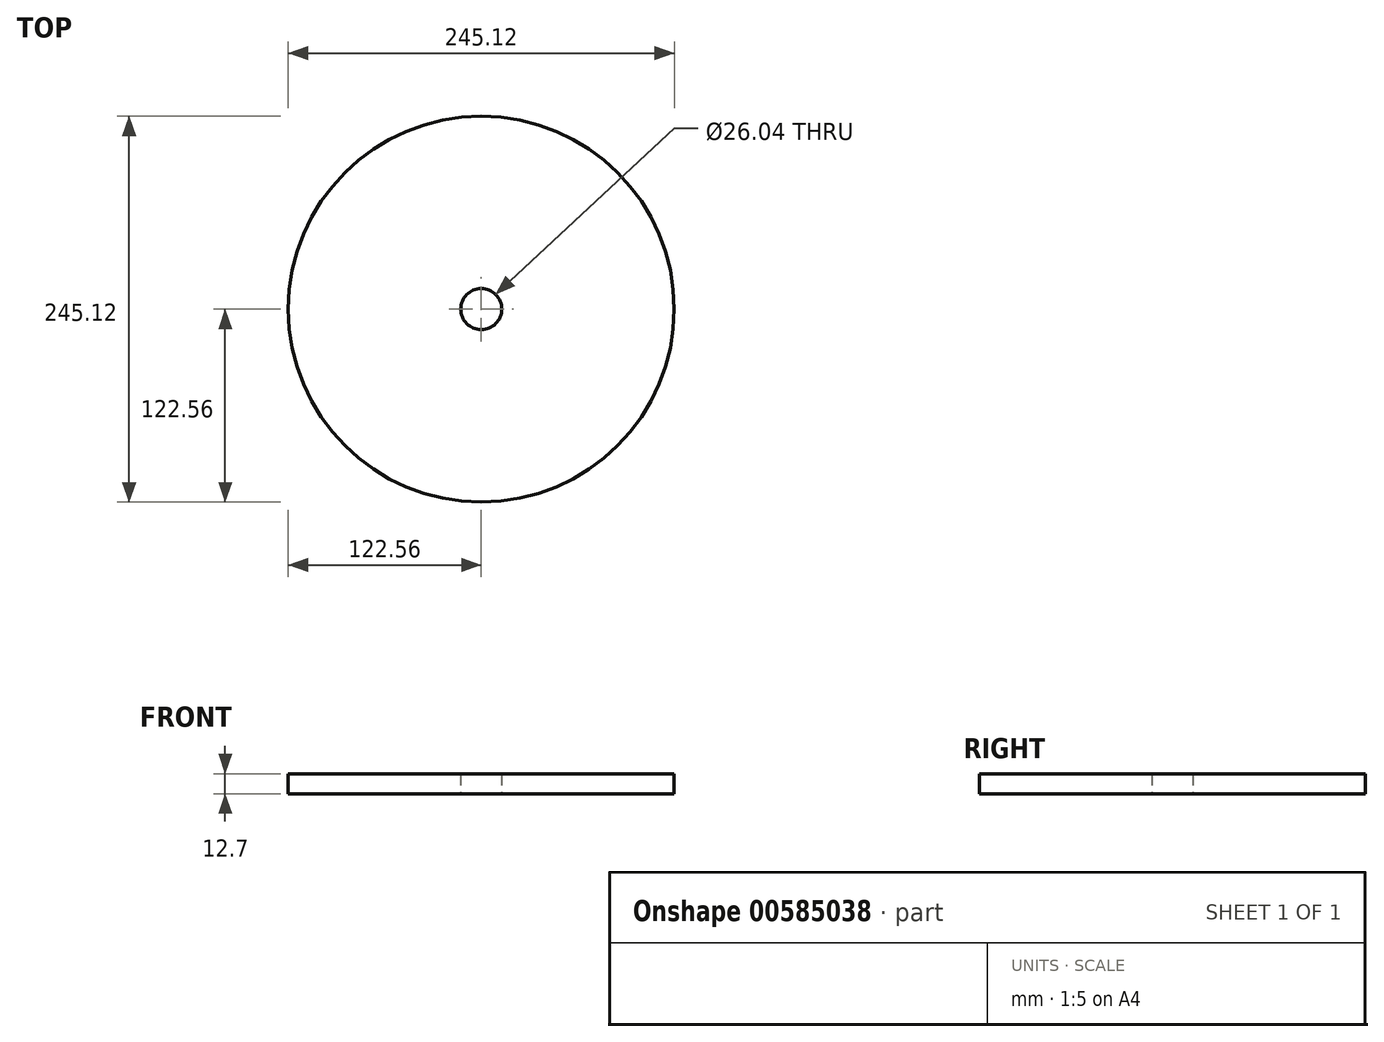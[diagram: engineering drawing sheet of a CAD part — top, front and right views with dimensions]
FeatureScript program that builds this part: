
annotation { "Feature Type Name" : "Feature", "Feature Type Description" : "" }
export const myFeature = defineFeature(function(context is Context, id is Id, definition is map)
    precondition{}
    {
        {
            var Q0;
            Q0=qCreatedBy(makeId("Top.planeOp"),FACE);
            var sketch = newSketch(context, id + "F0", { "sketchPlane" : qUnion([Q0])});
            skCircle(sketch, "E0", {"center": v(0, 0) * mm, "radius": 122.56 * mm});
            skCircle(sketch, "E1", {"center": v(0, 0) * mm, "radius": 13.02 * mm});
            skSolve(sketch);
        }
        {
            var Q0;
            Q0 = qSketchRegion(id + "F0", true);
            extrude(context, id + "F1", {"entities" : qUnion([Q0]), "depth" : 12.7 * mm, "offsetDistance" : 25.4 * mm});
        }
    });
